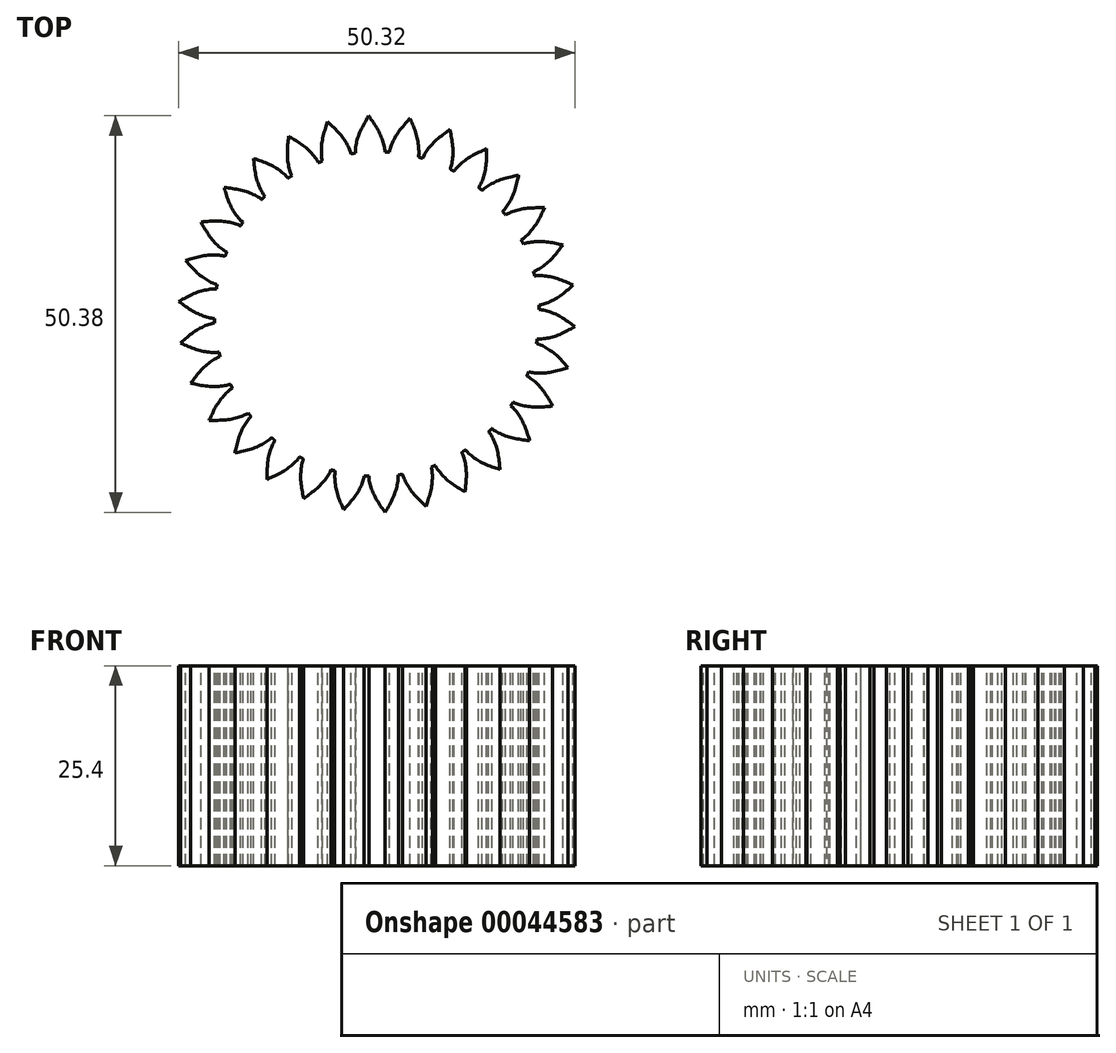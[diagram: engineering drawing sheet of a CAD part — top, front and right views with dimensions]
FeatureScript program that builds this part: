
annotation { "Feature Type Name" : "Feature", "Feature Type Description" : "" }
export const myFeature = defineFeature(function(context is Context, id is Id, definition is map)
    precondition{}
    {
        {
            assignVariable(context, id + "F0", {"name" : "nt", "anyValue" : 30});
        }
        {
            var Q0;
            Q0=qCreatedBy(makeId("Top.planeOp"),FACE);
            var sketch = newSketch(context, id + "F1", { "sketchPlane" : qUnion([Q0])});
            skPoint(sketch, "E0", {"position": v(1.08, 20.6) * mm});
            skPoint(sketch, "E1", {"position": v(1.06, 20.92) * mm});
            skPoint(sketch, "E2", {"position": v(0.84, 21.88) * mm});
            skPoint(sketch, "E3", {"position": v(0.2, 23.39) * mm});
            skPoint(sketch, "E4", {"position": v(-1.05, 25.3) * mm});
            skCircle(sketch, "E5", {"center": v(0, 0) * mm, "radius": 20.62 * mm});
            skCircle(sketch, "E6", {"center": v(0, 0) * mm, "radius": 23.81 * mm, "construction": true});
            skCircle(sketch, "E7", {"center": v(0, 0) * mm, "radius": 30.2 * mm});
            skCircle(sketch, "E8", {"center": v(0, 0) * mm, "radius": 25.33 * mm});
            skFitSpline(sketch, "E9", {"points": [v(1.08, 20.6) * mm, v(1.06, 20.92) * mm, v(0.84, 21.88) * mm, v(0.2, 23.39) * mm, v(-1.05, 25.3) * mm], "startDerivative": vector(-0.05, 2.19) * mm, "endDerivative": vector(-3.92, 5.61) * mm});
            skLineSegment(sketch, "E10", {"start": v(-1.05, 25.3) * mm, "end": v(-0.85, 20.6) * mm});
            skSolve(sketch);
        }
        {
            var Q0;
            {var subQ1=sQuery(id+"F1.wireOp",EDGE,"E9");Q0=makeQuery(id+"F1.imprint","IMPRINT",FACE,{"disambiguationData":[TD([[makeQuery(id+"F1.imprint","IMPRINT",EDGE,{"derivedFrom":subQ1}),1.0]])]});}
            extrude(context, id + "F2", {"entities" : qUnion([Q0]), "depth" : 25.4 * mm});
        }
        {
            var Q0;
            Q0=makeQuery(id+"F2.opExtrude","CAP_FACE",FACE,{"disambiguationData":[OSD([sQuery(id+"F1.wireOp",EDGE,"E5"),sQuery(id+"F1.wireOp",EDGE,"E9"),sQuery(id+"F1.wireOp",EDGE,"E10")])],"isStart":false});
            var sketch = newSketch(context, id + "F3", { "sketchPlane" : qUnion([Q0])});
            skFitSpline(sketch, "E11.0", {"points": [v(1.08, 20.6) * mm, v(1.08, 20.69) * mm, v(1.07, 20.95) * mm, v(0.85, 21.96) * mm, v(0.25, 23.46) * mm, v(-0.6, 24.66) * mm, v(-1.05, 25.3) * mm]});
            skFitSpline(sketch, "E12.0", {"points": [v(1.02, 20.6) * mm, v(1.01, 20.68) * mm, v(1.01, 20.86) * mm, v(0.92, 21.34) * mm, v(0.76, 21.93) * mm, v(0.54, 22.56) * mm, v(0.24, 23.2) * mm, v(-0.15, 23.88) * mm, v(-0.6, 24.57) * mm, v(-0.94, 25.04) * mm, v(-1.1, 25.27) * mm]});
            skLineSegment(sketch, "E13", {"start": v(-1.05, 25.3) * mm, "end": v(-1.1, 25.27) * mm});
            skLineSegment(sketch, "E14", {"start": v(1.08, 20.6) * mm, "end": v(1.02, 20.6) * mm});
            skSolve(sketch);
        }
        {
            var Q0;
            {var subQ3=sQuery(id+"F3.wireOp",EDGE,"E11.0");Q0=makeQuery(id+"F3.imprint","IMPRINT",FACE,{"disambiguationData":[TD([[makeQuery(id+"F3.imprint","IMPRINT",EDGE,{"derivedFrom":subQ3}),1.0]])]});}
            extrude(context, id + "F4", {"entities" : qUnion([Q0]), "operationType" : NewBodyOperationType.REMOVE, "endBound" : BoundingType.THROUGH_ALL, "oppositeDirection" : true, "depth" : 25.4 * mm});
        }
        {
            var Q0;
            Q0=makeQuery(id+"F2.opExtrude","SWEPT_BODY",BODY,{"disambiguationData":[OSD([sQuery(id+"F1.wireOp",EDGE,"E5"),sQuery(id+"F1.wireOp",EDGE,"E9"),sQuery(id+"F1.wireOp",EDGE,"E10")])]});
            var Q1;
            Q1=makeQuery(id+"F2.opExtrude","SWEPT_FACE",FACE,{"disambiguationData":[OSD([sQuery(id+"F1.wireOp",EDGE,"E10")])]});
            mirror(context, id + "F5", {"operationType" : NewBodyOperationType.ADD, "entities" : qUnion([Q0]), "mirrorPlane" : qUnion([Q1])});
        }
        {
            var Q0;
            {var subQ0=makeQuery(id+"F2.opExtrude","CAP_FACE",FACE,{"disambiguationData":[OSD([sQuery(id+"F1.wireOp",EDGE,"E5"),sQuery(id+"F1.wireOp",EDGE,"E9"),sQuery(id+"F1.wireOp",EDGE,"E10")])],"isStart":false});Q0=makeQuery(id+"F5.boolean.opBoolean","MERGE",FACE,{"derivedFrom":[subQ0,makeQuery(id+"F5.opPattern","COPY",FACE,{"derivedFrom":subQ0,"instanceName":"1"})]});}
            var sketch = newSketch(context, id + "F6", { "sketchPlane" : qUnion([Q0])});
            skCircle(sketch, "E15", {"center": v(0, 0) * mm, "radius": 20.62 * mm});
            skSolve(sketch);
        }
        {
            var Q0;
            Q0 = qSketchRegion(id + "F6", true);
            var Q1;
            {var subQ0=makeQuery(id+"F2.opExtrude","CAP_FACE",FACE,{"disambiguationData":[OSD([sQuery(id+"F1.wireOp",EDGE,"E5"),sQuery(id+"F1.wireOp",EDGE,"E9"),sQuery(id+"F1.wireOp",EDGE,"E10")])],"isStart":true});Q1=makeQuery(id+"F5.boolean.opBoolean","MERGE",FACE,{"derivedFrom":[subQ0,makeQuery(id+"F5.opPattern","COPY",FACE,{"derivedFrom":subQ0,"instanceName":"1"})]});}
            extrude(context, id + "F7", {"entities" : qUnion([Q0]), "endBound" : BoundingType.UP_TO_SURFACE, "oppositeDirection" : true, "endBoundEntityFace" : qUnion([Q1]), "depth" : 25.4 * mm});
        }
        {
            var Q0;
            Q0=makeQuery(id+"F2.opExtrude","SWEPT_BODY",BODY,{"disambiguationData":[OSD([sQuery(id+"F1.wireOp",EDGE,"E5"),sQuery(id+"F1.wireOp",EDGE,"E9"),sQuery(id+"F1.wireOp",EDGE,"E10")])]});
            var Q1;
            {var subQ0=makeQuery(id+"F2.opExtrude","SWEPT_FACE",FACE,{"disambiguationData":[OSD([sQuery(id+"F1.wireOp",EDGE,"E5")])]});Q1=makeQuery(id+"F5.boolean.opBoolean","MERGE",FACE,{"derivedFrom":[subQ0,makeQuery(id+"F5.opPattern","COPY",FACE,{"derivedFrom":subQ0,"instanceName":"1"})]});}
            circularPattern(context, id + "F8", {"operationType" : NewBodyOperationType.ADD, "entities" : qUnion([Q0]), "axis" : qUnion([Q1]), "angle" : 360 * degree, "instanceCount" : getVariable(context, 'nt'), "equalSpace" : true});
        }
    });
